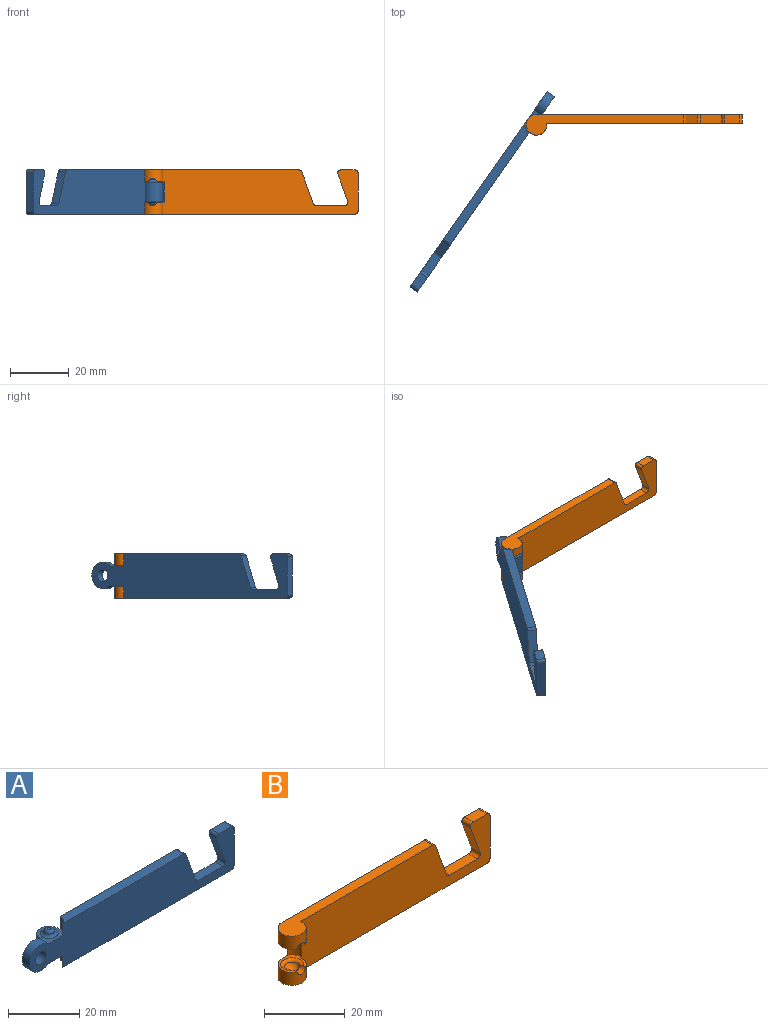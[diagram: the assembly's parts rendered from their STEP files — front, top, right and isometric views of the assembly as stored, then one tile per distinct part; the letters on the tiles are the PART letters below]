
ASSEMBLY  parts=2 mates=1
PART A: 29 faces, bbox 81.3x7x15 mm
  f0: plane 48x3mm, normal (0,0,1), area 139.9mm2, adj f1,f3,f14,f23
  f1: plane 66.54x15mm, normal (0,1,0), area 849.5mm2, adj f0,f4,f5,f6,f7,f8,f12,f13
  f2: plane 9x7.84mm, normal (0,1,0), area 44.5mm2, adj f6,f8,f13,f27,f28
  f3: plane 81.3x15mm, normal (0,-1,0), area 957.7mm2, adj f0,f4,f5,f6,f7,f12,f13,f14
  f4: plane 67.06x3mm, normal (0,0,-1), area 197.1mm2, adj f1,f3,f7,f26
  f5: plane 13x3mm, normal (1,0,0), area 39mm2, adj f1,f3,f25,f26
  f6: plane 8.07x7mm, normal (0,0,-1), area 25.3mm2, adj f1,f2,f3,f7,f8,f10,f27
  f7: cylinder r=4mm len=4.1mm, axis (0,0,1), area 15.4mm2, adj f1,f3,f4,f6
  f8: cylinder r=3.5mm len=7mm, axis (0,0,1), area 81.6mm2, adj f1,f2,f6,f13
  f9: plane 1.05x1.05mm, normal (0,0,-1), area 0.9mm2, adj f11
  f10: torus R=2.5mm, axis (0,0,-1), area 17mm2, adj f6,f11
  f11: torus R=0.52mm, axis (0,0,1), area 10mm2, adj f9,f10
  f12: plane 4.94x3mm, normal (0,0,1), area 14.8mm2, adj f1,f3,f24,f25
  f13: plane 7.6x7mm, normal (0,0,1), area 23.9mm2, adj f1,f2,f3,f8,f14,f16,f27
  f14: cylinder r=4mm len=4.1mm, axis (0,0,-1), area 15.4mm2, adj f0,f1,f3,f13
  f15: plane 1.05x1.05mm, normal (0,0,1), area 0.9mm2, adj f17
  f16: torus R=2.5mm, axis (0,0,1), area 17mm2, adj f13,f17
  f17: torus R=0.52mm, axis (0,0,-1), area 10mm2, adj f15,f16
  f18: plane 9.32x3.39mm, normal (-0.94,0,-0.34), area 29.7mm2, adj f1,f3,f22,f24
  f19: plane 10.68x3.89mm, normal (0.94,0,0.34), area 34.1mm2, adj f1,f3,f21,f23
  f20: plane 9.87x3mm, normal (0,0,1), area 29.6mm2, adj f1,f3,f21,f22
  f21: cylinder r=1mm len=3mm, axis (0,1,0), area 3.7mm2, adj f1,f3,f19,f20
  f22: cylinder r=1mm len=3mm, axis (0,1,0), area 5.8mm2, adj f1,f3,f18,f20
  f23: cylinder r=1mm len=3mm, axis (0,1,0), area 3.7mm2, adj f0,f1,f3,f19
  f24: cylinder r=1mm len=3mm, axis (0,1,0), area 5.8mm2, adj f1,f3,f12,f18
  f25: cylinder r=1mm len=3mm, axis (0,-1,0), area 4.7mm2, adj f1,f3,f5,f12
  f26: cylinder r=1mm len=3mm, axis (0,-1,0), area 4.7mm2, adj f1,f3,f4,f5
  f27: cylinder r=4.5mm len=9mm, axis (0,1,0), area 61.6mm2, adj f2,f3,f6,f13
  f28: cylinder r=2.15mm len=4.3mm, axis (0,1,0), area 40.5mm2, adj f2,f3
PART B: 30 faces, bbox 73.8x7.3x15 mm
  f0: plane 66.54x15mm, normal (0,-1,0), area 850.1mm2, adj f2,f4,f5,f6,f7,f8,f14,f15
  f1: plane 70x15mm, normal (0,1,0), area 892mm2, adj f2,f4,f5,f6,f7,f8,f14,f15
  f2: plane 53.43x7mm, normal (0,0,1), area 180.4mm2, adj f0,f1,f14,f25
  f3: plane 0.2x0.15mm, normal (0,-1,0), area 0mm2, adj f9,f11,f12
  f4: cylinder r=3.5mm len=7mm, axis (0,0,-1), area 65.3mm2, adj f0,f1,f5,f6,f9
  f5: plane 7.47x6.68mm, normal (0,0,1), area 13.3mm2, adj f0,f1,f4,f8,f9,f12
  f6: plane 72.5x7mm, normal (0,0,-1), area 237.6mm2, adj f0,f1,f4,f29
  f7: plane 13x3mm, normal (1,0,0), area 39mm2, adj f0,f1,f28,f29
  f8: cylinder r=4mm len=7mm, axis (0,0,-1), area 26.3mm2, adj f0,f1,f5,f15
  f9: cylinder r=1.5mm len=2.94mm, axis (0,1,0), area 7.2mm2, adj f3,f4,f5,f10,f11,f12
  f10: plane 0.2x0.15mm, normal (0,-1,0), area 0mm2, adj f9,f11,f12
  f11: sphere r=2mm, area 15.8mm2, adj f3,f9,f10,f12
  f12: torus R=2.83mm, axis (0,0,1), area 14mm2, adj f3,f5,f9,f10,f11
  f13: plane 0.2x0.15mm, normal (0,-1,0), area 0mm2, adj f17,f19,f20
  f14: cylinder r=3.5mm len=7mm, axis (0,0,1), area 65.3mm2, adj f0,f1,f2,f15,f17
  f15: plane 7.47x6.68mm, normal (0,0,-1), area 13.3mm2, adj f0,f1,f8,f14,f17,f20
  f16: plane 4.94x3mm, normal (0,0,1), area 14.8mm2, adj f0,f1,f24,f28
  f17: cylinder r=1.5mm len=2.94mm, axis (0,1,0), area 7.2mm2, adj f13,f14,f15,f18,f19,f20
  f18: plane 0.2x0.15mm, normal (0,-1,0), area 0mm2, adj f17,f19,f20
  f19: sphere r=2mm, area 15.8mm2, adj f13,f17,f18,f20
  f20: torus R=2.83mm, axis (0,0,-1), area 14mm2, adj f13,f15,f17,f18,f19
  f21: plane 9.87x3mm, normal (0,0,1), area 29.6mm2, adj f0,f1,f26,f27
  f22: plane 9.32x3.39mm, normal (-0.94,0,-0.34), area 29.7mm2, adj f0,f1,f24,f27
  f23: plane 10.68x3.89mm, normal (0.94,0,0.34), area 34.1mm2, adj f0,f1,f25,f26
  f24: cylinder r=1mm len=3mm, axis (0,1,0), area 5.8mm2, adj f0,f1,f16,f22
  f25: cylinder r=1mm len=3mm, axis (0,1,0), area 3.7mm2, adj f0,f1,f2,f23
  f26: cylinder r=1mm len=3mm, axis (0,1,0), area 3.7mm2, adj f0,f1,f21,f23
  f27: cylinder r=1mm len=3mm, axis (0,1,0), area 5.8mm2, adj f0,f1,f21,f22
  f28: cylinder r=1mm len=3mm, axis (0,1,0), area 4.7mm2, adj f0,f1,f7,f16
  f29: cylinder r=1mm len=3mm, axis (0,1,0), area 4.7mm2, adj f0,f1,f6,f7
PLACE A rot(axis=(0,0,-1),125.1deg) t=(0.09,-37.51,-1.47)mm
PLACE B t=(44.96,1.82,-1.47)mm
MATE revolute A.f7 <-> B.f4  axis (0,0,1) through (9.96,-1.68,6.03)mm
